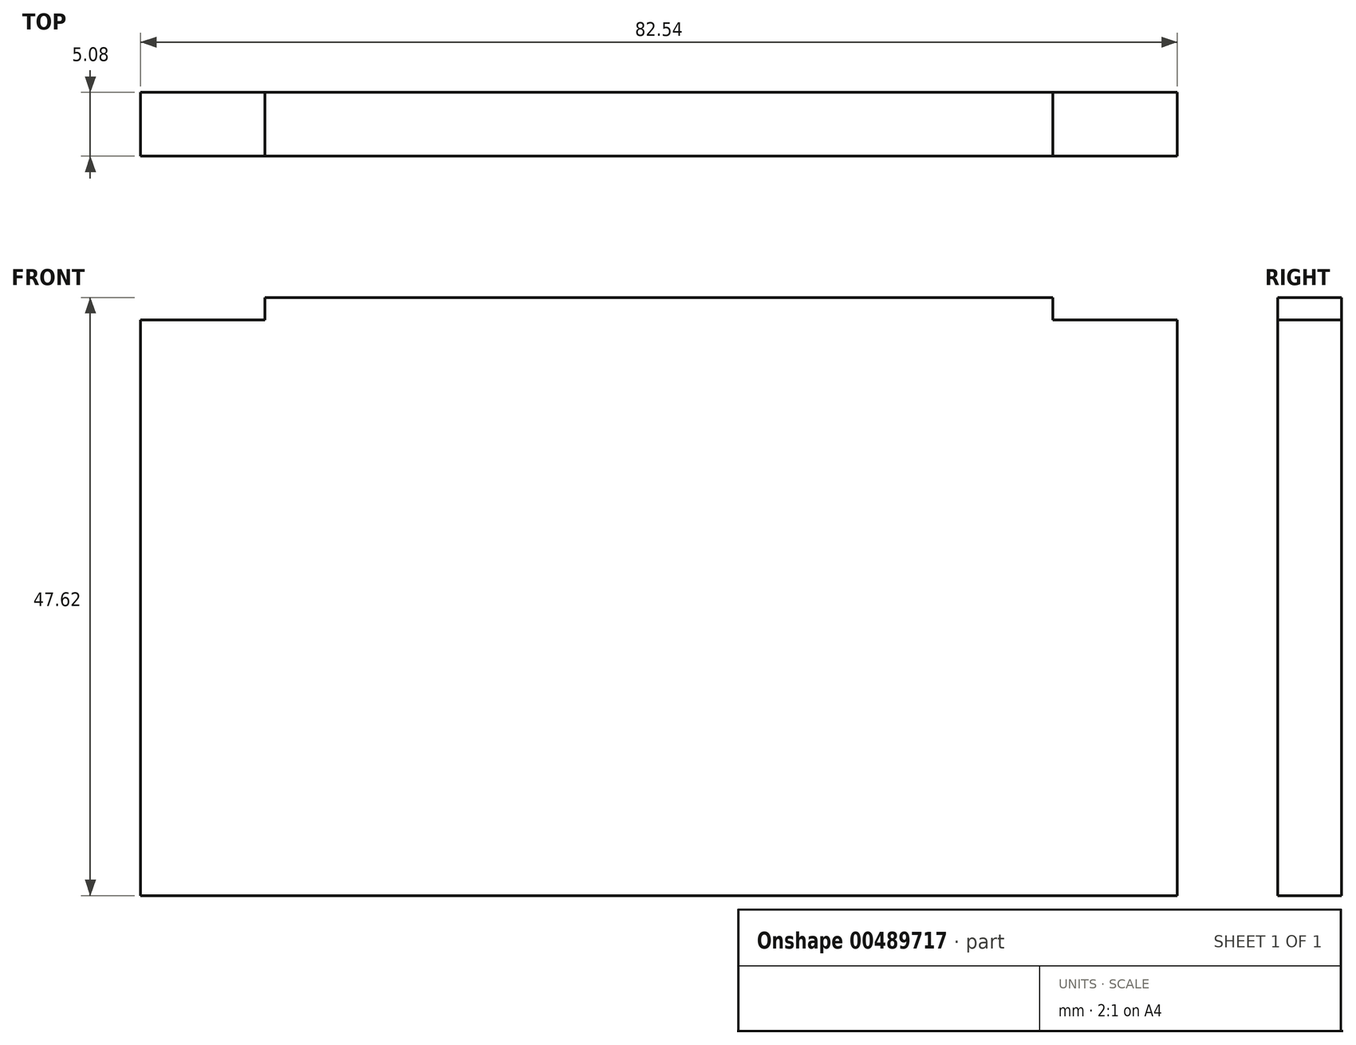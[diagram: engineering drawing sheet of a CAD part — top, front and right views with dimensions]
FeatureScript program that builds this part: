
annotation { "Feature Type Name" : "Feature", "Feature Type Description" : "" }
export const myFeature = defineFeature(function(context is Context, id is Id, definition is map)
    precondition{}
    {
        {
            var Q0;
            Q0=qCreatedBy(makeId("Front.planeOp"),FACE);
            var sketch = newSketch(context, id + "F0", { "sketchPlane" : qUnion([Q0])});
            skLineSegment(sketch, "E0.bottom", {"start": v(41.28, 22.92) * mm, "end": v(31.37, 22.92) * mm});
            skLineSegment(sketch, "E0.top", {"start": v(41.27, -22.92) * mm, "end": v(-41.28, -22.92) * mm});
            skLineSegment(sketch, "E0.left", {"start": v(41.28, 22.92) * mm, "end": v(41.27, -22.92) * mm});
            skLineSegment(sketch, "E0.right", {"start": v(-41.27, 22.92) * mm, "end": v(-41.28, -22.92) * mm});
            skPoint(sketch, "E0.middle", {"position": v(0, 0) * mm});
            skLineSegment(sketch, "E1.bottom", {"start": v(-41.27, 22.92) * mm, "end": v(-31.37, 22.92) * mm});
            skLineSegment(sketch, "E1.left", {"start": v(-41.27, 22.92) * mm, "end": v(-41.27, 16.61) * mm});
            skLineSegment(sketch, "E2", {"start": v(-31.37, 22.92) * mm, "end": v(-31.37, 24.7) * mm});
            skLineSegment(sketch, "E3", {"start": v(31.37, 22.92) * mm, "end": v(31.37, 24.7) * mm});
            skLineSegment(sketch, "E4", {"start": v(-31.37, 24.7) * mm, "end": v(31.37, 24.7) * mm});
            skLineSegment(sketch, "E5.trimOffspring", {"start": v(-31.37, 22.92) * mm, "end": v(-41.27, 22.92) * mm});
            skSolve(sketch);
        }
        {
            var Q0;
            Q0 = qSketchRegion(id + "F0", true);
            extrude(context, id + "F1", {"entities" : qUnion([Q0]), "depth" : 5.08 * mm});
        }
    });
